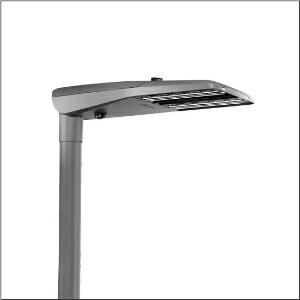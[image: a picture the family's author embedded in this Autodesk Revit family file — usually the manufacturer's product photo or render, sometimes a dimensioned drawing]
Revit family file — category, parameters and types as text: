
# Revit family: streetlight_sl_11_iq_midi___pc-l_5xc3e11y08me_a024
name_source: partatom
category: Lighting Fixtures
units: mm (PartAtom-declared; Revit-internal decimal feet)

## family parameters
Cut with Voids When Loaded = No
Host = Face
Light Source = No
Part Type = Normal
Room Calculation Point = No
Round Connector Dimension = Use Diameter
Shared = No

## types (1)
- --- (1 x LED, 9610 lm, 123.4 W, 1800K)
    Apparent Load = 123 VA
    CIE Flux Codes = 37 73 96 100 100
    Color Rendering = 70
    Color Temperature = 1800K
    Default Elevation = 1800 mm
    Description = Streetlight SL 11 iQ midi, mast luminaire, primary light control with 3 zone facetted reflector, of plastic, silver coated, highly specular, primary optical cover: cover, of PMMA, transparent, light distribution: PC-L, light emission: direct distribution, primary light characteristic: asymmetric, left, installation type: post-top, side-entry, LED, High Power LED, rated luminous flux: 9.610lm, luminous efficacy: 78lm/W, light colour: 718, colour temperature: 1800K, control: pre-setting: logarithmic dimming characteristic, Street-Remote, Auto-Match, Temp-Guard, Lumen-Switch, Night-Set, Smart-Wire, Light-Fading, Desk-Remote (wireless, voltage-free reading and setting of iQ features in the workshop via application-optimized NFC function/RFID function), optimised constant luminous flux control (CLO 2.0), with cable H07RN-F 5x 1.5mm², mains connection: 230..240V, AC, 50/60Hz, connection cable pre-assembled, cable length: 12,5m, start of lifetime: 123W, end of service life: 131W, reduction: 54W, luminaire housing, of diecast aluminium, powder-coated, Siteco® metallic grey (DB 702S), please order mast flange separately, inclination adjustable without tools: 0°, 5°, 10°, 15° (post-top) | 0°, -5°, -10°, -15° (side-entry), sealing non-destructively replaceable, multi-level sealing system, length: 780mm, width: 376mm, height: 118mm, mast flange for spigot size: 42mm (side-entry): 5XC10008XM4, 60/48mm (side-entry/post-top): 5XC10108XM2, 76/60mm (side-entry/post-top): 5XC10108XM1, equipment: Power, Smart Interface below and above, protection rating (complete): IP66, insulation class (complete): insulation class II (safety insulation), certification: CE, ENEC, VDE, UKCA, impact resistance: IK09, permissible operating ambient temperature for outdoor applications: -25..+50°C, standard-compliant lighting for roads and squares, Environmental Product Declaration (EPD) tested and certified by an independent institute, packaging unit: 1 piece

Light Distribution: PC-L
    Height = 118 mm
    Lamp = 1 x LED
    Lamp Light Flux = 9610 lm
    Lamp Power = 123.4 W
    Lamp count = 1
    Length = 780 mm
    Luminous efficacy = 78 lm/W
    Manufacturer = Siteco
    ModVariant = No
    Model = 5XC3E11Y08ME
    Number of Poles = 1
    OnlyDefault = Yes
    Power Factor = 1
    Product Name = Streetlight SL 11 iQ midi | PC-L
    Product group = mast luminaire | pylon top
    ProductGroupID = 6100
    Protection Class = Protection class II
    Protection Degree = IP 66
    RLX_Detail_Level = 1
    RLX_Emergency_Light_Flux = 0 lm
    RLX_Emergency_Type = 0
    RLX_Emergency_Type_DB = No
    RlxData = <blob elided: 73569 chars, md5=18259c66>
    Socket = socket
    Standby Power = 0 W
    System Light Flux = 9610 lm
    System Power = 123 W
    Type Comments = factory setting: luminous flux: 100 % | dim-lin: 254 | 553 mA
    Type Image = l_1004429.jpg
    URL = http://relux.com
    VarID = @adj_000953
    Voltage = 0 V
    Weight = 0.00 kg
    Width = 376 mm

## geometry (parser evidence)
native form markers: Blend x4, Sweep x10
no freeform markers — native parametric forms only
